# Revit family: H-3010_RFA
name_source: partatom
category: Aparatos sanitarios
units: mm (PartAtom-declared; Revit-internal decimal feet)

## family parameters
Activar corte en vistas = No
Compartido = Sí
Corte con vacíos al cargar = No
Cota de conector redondo = Usar diámetro
Mantener orientación de anotación = No
Número OmniClass = 23.45.05.14.17
Punto de cálculo de habitación = Sí
Se basa en plano de trabajo = Sí
Siempre vertical = Sí
Tipo de pieza = Normal
Título OmniClass = Showers

## types (1)
- H-3010
    Brass Chromed = Brass
    Comentarios de tipo = Regadera de Plato Ancho de 12"
    Descripción = Regadera de Plato Ancho de 12" Chorro Fijo con Sistema Anticalcareo
    Elevación por defecto = 1"
    Fabricante = HELVEX S.A. de C.V.
    Garantía = El producto HELVEX esta garantizado como libre de defectos en materiales y procesos de
fabricacion. El producto HELVEX esta garantizado, en lo que
se refiere a los acabados; por un periodo de 10 años en los acabados cromo y duravex, y por 2
años en cabados diferentes al cromo, a partir de la fecha de compra indicada en la factura.
    Imagen de tipo = H-3010.jpg
    Inlet Threads = ½" - 14 NPT
    Max. Water Flow = 2.2 gal/min
    Max. Working Pressure = 85.3 psi
    Min. Working Pressure = 14.2 psi
    Modelo = H-3010
    URL = https://helvex.com.mx

## geometry (parser evidence)
native form markers: Sweep x3
no freeform markers — native parametric forms only
